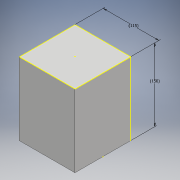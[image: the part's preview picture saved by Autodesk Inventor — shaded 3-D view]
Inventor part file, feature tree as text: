
AUTODESK INVENTOR PART (.ipt)
format: ipt  version: 2017 (Build 210142000, 142)  size: 95,744 bytes
history: native  units: mm
features: sketch x3, extrude x1, projected_geometry x1
ambient origin geometry x8: Origin, YZ Plane, XZ Plane, XY Plane, X Axis, Y Axis, Z Axis, Center Point
bodies: Solid1 (feature_tree)
feature tree (5):
  extrude  "Extrusion1"  Depth=115.0mm
  sketch  "Sketch2"  dims[d2=150.0mm d3=0.0mm]
  sketch  "Sketch3"  dims[d4=115.0mm d5=150.0mm]
  sketch  "Sketch1"  dims[d0=115.0mm d1=115.0mm]
  projected_geometry  "Projected Loop1"
